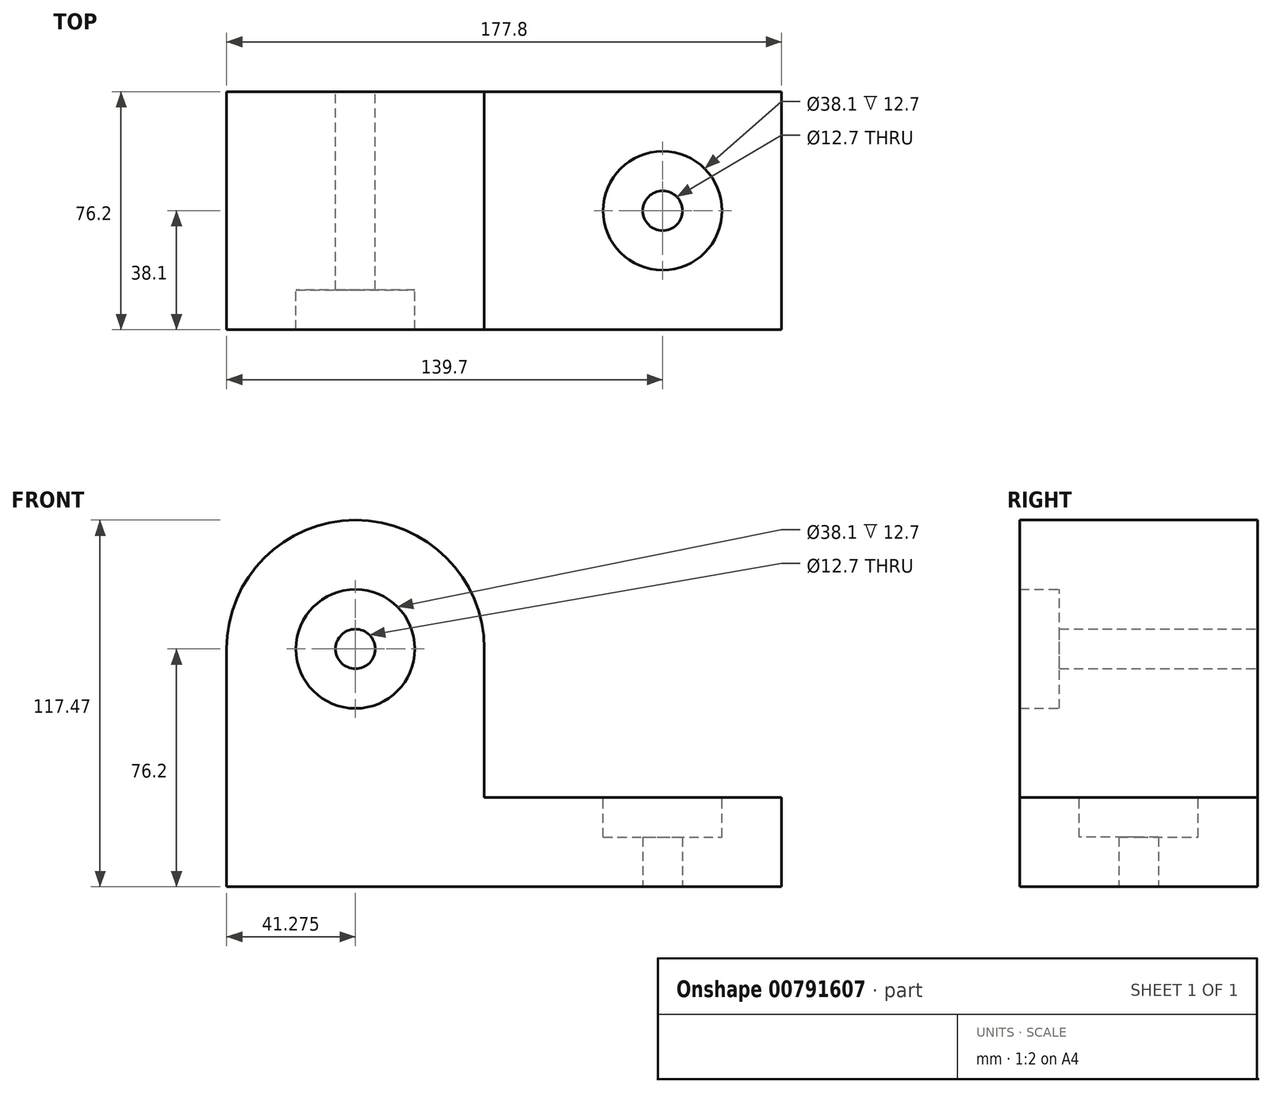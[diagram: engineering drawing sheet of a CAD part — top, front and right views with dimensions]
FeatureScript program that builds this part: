
annotation { "Feature Type Name" : "Feature", "Feature Type Description" : "" }
export const myFeature = defineFeature(function(context is Context, id is Id, definition is map)
    precondition{}
    {
        {
            var Q0;
            Q0=qCreatedBy(makeId("Front.planeOp"),FACE);
            var sketch = newSketch(context, id + "F0", { "sketchPlane" : qUnion([Q0])});
            skLineSegment(sketch, "E0", {"start": v(0, 0) * mm, "end": v(177.8, 0) * mm});
            skLineSegment(sketch, "E1", {"start": v(177.8, 0) * mm, "end": v(177.8, 28.57) * mm});
            skLineSegment(sketch, "E2", {"start": v(0, 0) * mm, "end": v(0, 76.2) * mm});
            skLineSegment(sketch, "E3", {"start": v(0, 76.2) * mm, "end": v(82.55, 76.2) * mm});
            skLineSegment(sketch, "E4", {"start": v(82.55, 76.2) * mm, "end": v(82.55, 28.57) * mm});
            skLineSegment(sketch, "E5", {"start": v(82.55, 28.57) * mm, "end": v(177.8, 28.57) * mm});
            skArc(sketch, "E6", {"start": v(0, 76.2) * mm, "mid": v(41.28, 117.48) * mm, "end": v(82.55, 76.2) * mm});
            skCircle(sketch, "E7", {"center": v(41.28, 76.2) * mm, "radius": 19.05 * mm});
            skCircle(sketch, "E8", {"center": v(41.28, 76.2) * mm, "radius": 6.35 * mm});
            skSolve(sketch);
        }
        {
            var Q0;
            Q0=qSketchRegion(id+"F0",true);
            extrude(context, id + "F1", {"entities" : qUnion([Q0]), "depth" : 76.2 * mm, "offsetDistance" : 25.4 * mm});
        }
        {
            var Q0;
            {var subQ0=sQuery(id+"F0.wireOp",EDGE,"E7");var subQ1=sQuery(id+"F0.wireOp",EDGE,"E3");var subQ2=makeQuery(id+"F0.imprint","INTERSECT",VERTEX,{"disambiguationData":[OD(0.0)],"derivedFrom":[subQ1,subQ0]});Q0=makeQuery(id+"F0.imprint","IMPRINT",FACE,{"disambiguationData":[TD([[makeQuery(id+"F0.imprint","IMPRINT",EDGE,{"disambiguationData":[TD([[subQ2,-1.0]])],"derivedFrom":subQ1}),-1.0]])]});}
            var Q1;
            {var subQ0=sQuery(id+"F0.wireOp",EDGE,"E7");var subQ1=sQuery(id+"F0.wireOp",EDGE,"E3");var subQ2=makeQuery(id+"F0.imprint","INTERSECT",VERTEX,{"disambiguationData":[OD(0.0)],"derivedFrom":[subQ1,subQ0]});Q1=makeQuery(id+"F0.imprint","IMPRINT",FACE,{"disambiguationData":[TD([[makeQuery(id+"F0.imprint","IMPRINT",EDGE,{"disambiguationData":[TD([[subQ2,-1.0]])],"derivedFrom":subQ1}),1.0]])]});}
            extrude(context, id + "F2", {"entities" : qUnion([Q0, Q1]), "operationType" : NewBodyOperationType.ADD, "depth" : 63.5 * mm, "offsetDistance" : 25.4 * mm});
        }
        {
            var Q0;
            Q0=makeQuery(id+"F1.opExtrude","SWEPT_FACE",FACE,{"disambiguationData":[OSD([sQuery(id+"F0.wireOp",EDGE,"E5")])]});
            var sketch = newSketch(context, id + "F3", { "sketchPlane" : qUnion([Q0])});
            skLineSegment(sketch, "E9", {"start": v(177.8, -38.1) * mm, "end": v(139.7, -38.1) * mm, "construction": true});
            skCircle(sketch, "E10", {"center": v(139.7, -38.1) * mm, "radius": 19.05 * mm});
            skSolve(sketch);
        }
        {
            var Q0;
            Q0=makeQuery(id+"F3.imprint","IMPRINT",FACE,{"disambiguationData":[TD([[makeQuery(id+"F3.imprint","IMPRINT",EDGE,{"derivedFrom":sQuery(id+"F3.wireOp",EDGE,"E10")}),1.0]])]});
            extrude(context, id + "F4", {"entities" : qUnion([Q0]), "operationType" : NewBodyOperationType.REMOVE, "oppositeDirection" : true, "depth" : 127 * mm, "offsetDistance" : 25.4 * mm});
        }
        {
            var Q0;
            Q0=makeQuery(id+"F1.opExtrude","SWEPT_FACE",FACE,{"disambiguationData":[OSD([sQuery(id+"F0.wireOp",EDGE,"E0")])]});
            var sketch = newSketch(context, id + "F5", { "sketchPlane" : qUnion([Q0])});
            skLineSegment(sketch, "E11", {"start": v(177.8, 38.1) * mm, "end": v(139.7, 38.1) * mm});
            skLineSegment(sketch, "E12", {"start": v(139.7, 38.1) * mm, "end": v(120.65, 38.1) * mm});
            skCircle(sketch, "E13", {"center": v(139.7, 38.1) * mm, "radius": 19.05 * mm});
            skCircle(sketch, "E14", {"center": v(139.7, 38.1) * mm, "radius": 6.35 * mm});
            skSolve(sketch);
        }
        {
            var Q0;
            Q0=qSketchRegion(id+"F5",true);
            extrude(context, id + "F6", {"entities" : qUnion([Q0]), "operationType" : NewBodyOperationType.ADD, "depth" : -15.88 * mm, "offsetDistance" : 25.4 * mm});
        }
    });
